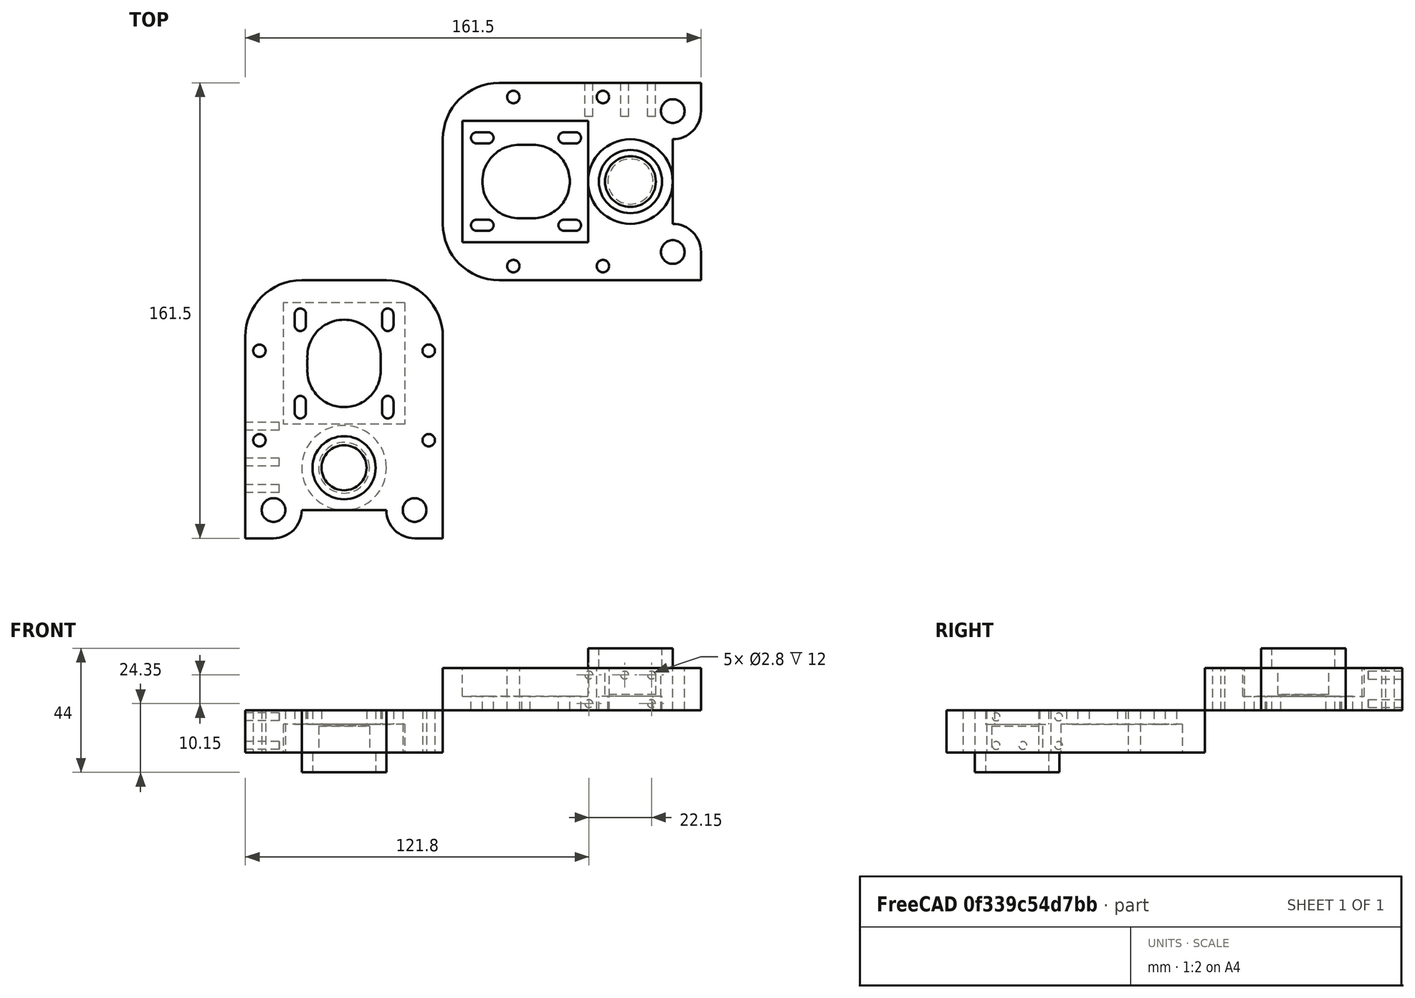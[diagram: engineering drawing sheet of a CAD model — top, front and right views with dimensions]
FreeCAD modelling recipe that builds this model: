
FCSTD DOCUMENT  (FreeCAD 0.15R4671 (Git))
Label: z_motor_holder
License: All rights reserved
LicenseURL: http://en.wikipedia.org/wiki/All_rights_reserved
objects: Part::Cylinder×20, Part::Cut×11, Part::MultiFuse×7, Part::Feature×5, Part::Box×5, Part::Fillet×2, Mesh::Feature×1
note: 50 computed .brp shape members not serialized (recipe doc carries the construction recipe); baked Part::Feature solids carry a one-line shape summary decoded from their .brp

FEATURE [Mesh::Feature] Zmotorholderantibacklash
FEATURE [Part::Feature] Zmotorholderantibacklash001001  label="Zmotorholderantibacklash002"
  shape: bbox 91.5 x 70 x 22 mm, 2151 faces, 0 solids (baked)
FEATURE [Part::Box] Box  label="Cubo"
  Height = 15
  Length = 91.5
  Width = 70
FEATURE [Part::Box] Box001  label="Cubo001"
  Height = 15
  Length = 10
  Placement = pos=(81.5,20,0) rot=(0,0,1;0rad)
  Width = 30
FEATURE [Part::Cut] Cut
  Base = -> Box
  Tool = -> Box001
FEATURE [Part::Box] Box002  label="Cubo002"
  Height = 10
  Length = 44.5
  Placement = pos=(7,13.5,5) rot=(0,0,1;0rad)
  Width = 43
FEATURE [Part::Cylinder] Cylinder  label="Cilindro"
  Angle = 360
  Height = 7
  Placement = pos=(66.5,35,15) rot=(0,0,1;0rad)
  Radius = 15
FEATURE [Part::Cylinder] Cylinder001  label="Cilindro001"
  Angle = 360
  Height = 7
  Placement = pos=(66.5,35,15) rot=(0,0,1;0rad)
  Radius = 11.2
FEATURE [Part::Cut] Cut002
  Base = -> Cylinder
  Tool = -> Cylinder001
FEATURE [Part::Cylinder] Cylinder002  label="Cilindro002"
  Angle = 360
  Height = 10
  Placement = pos=(66.5,35,5.6) rot=(0,0,1;0rad)
  Radius = 9
FEATURE [Part::Cylinder] Cylinder003  label="Cilindro003"
  Angle = 360
  Height = 5
  Placement = pos=(66.5,35,0) rot=(0,0,1;0rad)
  Radius = 11.2
FEATURE [Part::Cylinder] Cylinder004  label="Cilindro004"
  Angle = 360
  Height = 5
  Placement = pos=(66.5,35,0) rot=(0,0,1;0rad)
  Radius = 8
FEATURE [Part::Cut] Cut004
  Base = -> Cylinder003
  Tool = -> Cylinder004
FEATURE [Part::Cylinder] Cylinder005  label="Cilindro005"
  Angle = 360
  Height = 17
  Placement = pos=(25,5,-1) rot=(0,0,1;0rad)
  Radius = 2.2
FEATURE [Part::Cylinder] Cylinder006  label="Cilindro006"
  Angle = 360
  Height = 17
  Placement = pos=(56.75,5,-1) rot=(0,0,1;0rad)
  Radius = 2.2
FEATURE [Part::Cylinder] Cylinder007  label="Cilindro007"
  Angle = 360
  Height = 17
  Placement = pos=(56.75,65,-1) rot=(0,0,1;0rad)
  Radius = 2.2
FEATURE [Part::Cylinder] Cylinder008  label="Cilindro008"
  Angle = 360
  Height = 17
  Placement = pos=(25,65,-1) rot=(0,0,1;0rad)
  Radius = 2.2
FEATURE [Part::MultiFuse] Fusion001  label="screw_holes"
  Shapes = -> [Cylinder005,Cylinder007,Cylinder008,Cylinder006]
FEATURE [Part::Cylinder] Cylinder009  label="Cilindro009"
  Angle = 360
  Height = 17
  Placement = pos=(81.5,10,-1) rot=(0,0,1;0rad)
  Radius = 4.2
FEATURE [Part::Cylinder] Cylinder010  label="Cilindro010"
  Angle = 360
  Height = 17
  Placement = pos=(81.5,60,-1) rot=(0,0,1;0rad)
  Radius = 4.2
FEATURE [Part::MultiFuse] Fusion002  label="rod_holes"
  Shapes = -> [Cylinder009,Cylinder010]
FEATURE [Part::Cylinder] Cylinder011  label="Cilindro011"
  Angle = 360
  Height = 7
  Placement = pos=(12,19.5,-1) rot=(0,0,1;0rad)
  Radius = 2
FEATURE [Part::Cylinder] Cylinder012  label="Cilindro012"
  Angle = 360
  Height = 7
  Placement = pos=(16,19.5,-1) rot=(0,0,1;0rad)
  Radius = 2
FEATURE [Part::Box] Box003  label="Cubo003"
  Height = 7
  Length = 4
  Placement = pos=(12,17.5,-1) rot=(0,0,1;0rad)
  Width = 4
FEATURE [Part::MultiFuse] Fusion003
  Shapes = -> [Cylinder011,Box003,Cylinder012]
FEATURE [Part::Feature] Fusion004
  Placement = pos=(0,31,0) rot=(0,0,1;0rad)
  shape: bbox 8 x 4 x 7 mm, 17 faces (baked)
FEATURE [Part::Feature] Fusion005
  Placement = pos=(31,0,0) rot=(0,0,1;0rad)
  shape: bbox 8 x 4 x 7 mm, 17 faces (baked)
FEATURE [Part::Feature] Fusion006
  Placement = pos=(31,31,0) rot=(0,0,1;0rad)
  shape: bbox 8 x 4 x 7 mm, 17 faces (baked)
FEATURE [Part::MultiFuse] Fusion007  label="motor_screw_holes"
  Shapes = -> [Fusion003,Fusion005,Fusion004,Fusion006]
FEATURE [Part::Cylinder] Cylinder015  label="Cilindro015"
  Angle = 360
  Height = 13
  Placement = pos=(73.95,58,2.35) rot=(-1,0,0;1.5708rad)
  Radius = 1.4
FEATURE [Part::Cylinder] Cylinder016  label="Cilindro016"
  Angle = 360
  Height = 13
  Placement = pos=(73.95,58,12.5) rot=(-1,0,0;1.5708rad)
  Radius = 1.4
FEATURE [Part::Cylinder] Cylinder017  label="Cilindro017"
  Angle = 360
  Height = 13
  Placement = pos=(64.45,58,12.5) rot=(-1,0,0;1.5708rad)
  Radius = 1.4
FEATURE [Part::Cylinder] Cylinder018  label="Cilindro018"
  Angle = 360
  Height = 13
  Placement = pos=(51.8,58,12.5) rot=(-1,0,0;1.5708rad)
  Radius = 1.4
FEATURE [Part::Cylinder] Cylinder019  label="Cilindro019"
  Angle = 360
  Height = 13
  Placement = pos=(51.8,58,2.35) rot=(-1,0,0;1.5708rad)
  Radius = 1.4
FEATURE [Part::MultiFuse] Fusion009  label="endstop_screw_holes"
  Shapes = -> [Cylinder015,Cylinder016,Cylinder017,Cylinder018,Cylinder019]
FEATURE [Part::Feature] Cut011  label="z_motor_holder001"
  Placement = pos=(0,0,0) rot=(0.707107,-0.707107,0;3.14159rad)
  shape: bbox 70 x 91.5 x 22 mm, 69 faces (baked)
FEATURE [Part::Cylinder] Cylinder020  label="Cilindro020"
  Angle = 360
  Height = 7
  Placement = pos=(27,35,-1) rot=(0,0,1;0rad)
  Radius = 13
FEATURE [Part::Cylinder] Cylinder021  label="Cilindro021"
  Angle = 360
  Height = 7
  Placement = pos=(32,35,-1) rot=(0,0,1;0rad)
  Radius = 13
FEATURE [Part::Box] Box005  label="Cubo005"
  Height = 7
  Length = 3
  Placement = pos=(28,22,-1) rot=(0,0,1;0rad)
  Width = 26
FEATURE [Part::MultiFuse] Fusion010  label="motor_hole001"
  Shapes = -> [Cylinder020,Cylinder021,Box005]
FEATURE [Part::Cut] Cut012
  Base = -> Cut
  Tool = -> Box002
FEATURE [Part::MultiFuse] Fusion
  Shapes = -> [Cut002,Cut012]
FEATURE [Part::Cut] Cut013
  Base = -> Fusion
  Tool = -> Cylinder002
FEATURE [Part::Cut] Cut014
  Base = -> Cut013
  Tool = -> Cut004
FEATURE [Part::Cut] Cut015
  Base = -> Cut014
  Tool = -> Fusion001
FEATURE [Part::Cut] Cut016
  Base = -> Cut015
  Tool = -> Fusion002
FEATURE [Part::Cut] Cut017
  Base = -> Cut016
  Tool = -> Fusion007
FEATURE [Part::Cut] Cut018
  Base = -> Cut017
  Tool = -> Fusion010
FEATURE [Part::Cut] Cut019
  Base = -> Cut018
  Tool = -> Fusion009
FEATURE [Part::Fillet] Fillet
  Base = -> Cut019
  Edges = 2 edges r=9.99: [Edge30,Edge35]
FEATURE [Part::Fillet] Fillet001
  Base = -> Fillet
  Edges = 2 edges r=20: [Edge35,Edge43]
